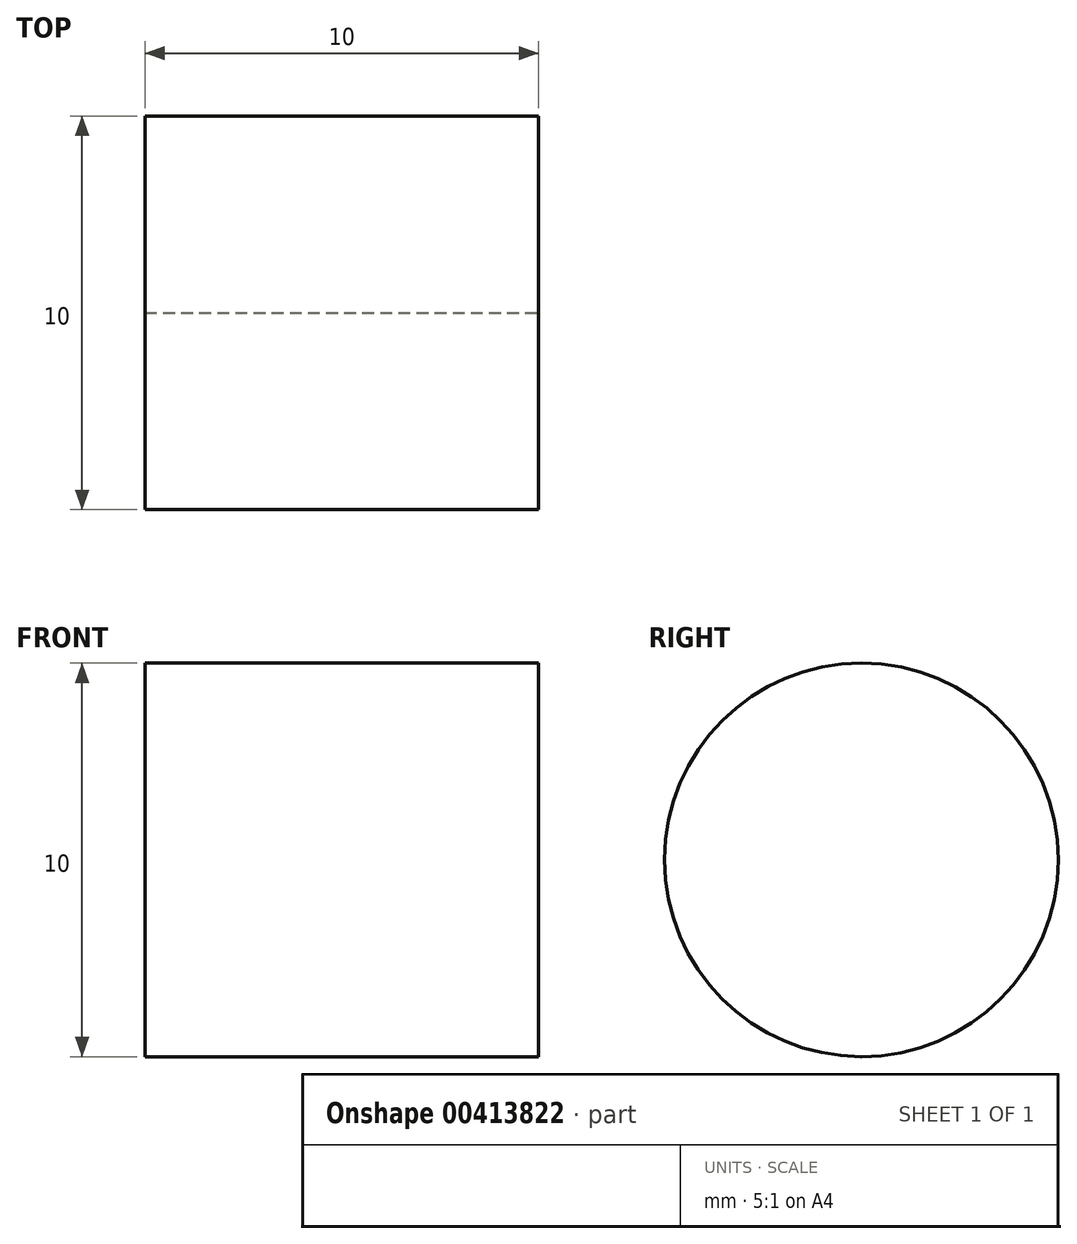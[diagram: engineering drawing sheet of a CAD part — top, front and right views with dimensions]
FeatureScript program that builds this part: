
annotation { "Feature Type Name" : "Feature", "Feature Type Description" : "" }
export const myFeature = defineFeature(function(context is Context, id is Id, definition is map)
    precondition{}
    {
        {
            var Q0;
            Q0=qCreatedBy(makeId("Right.planeOp"),FACE);
            var sketch = newSketch(context, id + "F0", { "sketchPlane" : qUnion([Q0])});
            skLineSegment(sketch, "E0", {"start": v(0, -5) * mm, "end": v(0, 5) * mm, "construction": true});
            skArc(sketch, "E1", {"start": v(0, -5) * mm, "mid": v(0, 5) * mm, "end": v(0, -5) * mm});
            skSolve(sketch);
        }
        {
            var Q0;
            Q0=sQuery(id+"F0.wireOp",EDGE,"E1");
            extrude(context, id + "F1", {"bodyType" : ToolBodyType.SURFACE, "surfaceEntities" : qUnion([Q0]), "depth" : 10 * mm});
        }
    });
